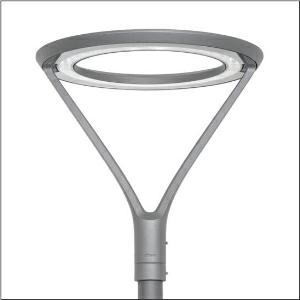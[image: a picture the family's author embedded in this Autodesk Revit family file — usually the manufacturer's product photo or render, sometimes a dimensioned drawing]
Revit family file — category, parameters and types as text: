
# Revit family: dl_r__20___st1_2a_5xa51283wa008_54be
name_source: partatom
category: Lighting Fixtures
units: mm (PartAtom-declared; Revit-internal decimal feet)

## family parameters
Cut with Voids When Loaded = No
Host = Face
Light Source = No
Part Type = Normal
Room Calculation Point = No
Round Connector Dimension = Use Diameter
Shared = No

## types (1)
- --- (1 x LED, 3040 lm, 24.6 W, 3000K)
    Apparent Load = 25 VA
    CIE Flux Codes = 32 72 97 100 100
    Color Rendering = 70
    Color Temperature = 3000K
    Default Elevation = 1800 mm
    Description = DL® 20, mast luminaire, primary light control with reflector, highly specular, primary optical cover: cover, of toughened safety glass of clear glass with excellent transmission level, light distribution: ST1.2a, light emission: direct distribution, primary light characteristic: asymmetric, installation type: post-top, LED, High Power LED, rated luminous flux: 3.020lm, luminous efficacy: 85lm/W, light colour: 730, colour temperature: 3000K, control gear: ECG Plus, control: overheat protection, power reduction, digital communication interface, constant luminous flux control, time-dependent luminous flux control, flexible luminous flux parameterisation, electronic power reduction, mains connection: 230..240V, 50/60Hz, connection cable pre-assembled, cable length: 5m, start of lifetime: 36W, end of service life: 36W, reduction: 17W, luminaire housing, upper part, of cast aluminium, powder-coated, Siteco® metallic grey (DB 702S), diameter: 690mm, height: 690mm, spigot size: 76mm (post-top), luminaire housing, of cast aluminium, powder-coated, Siteco® metallic grey (DB 702S), equipment: standard, protection rating (complete): IP66, insulation class (complete): insulation class II (safety insulation), certification: CE, ENEC, VDE, impact resistance: IK08, permissible operating ambient temperature: -25..+35°C, standard-compliant lighting for roads and squares, packaging unit: 1 piece

Light Distribution: ST1.2a
    Height = 690 mm
    Lamp = 1 x LED
    Lamp Light Flux = 3040 lm
    Lamp Power = 24.6 W
    Lamp count = 1
    Length = 690 mm
    Luminous efficacy = 124 lm/W
    Manufacturer = Siteco
    ModVariant = No
    Model = 5XA51283WA008
    Number of Poles = 1
    OnlyDefault = Yes
    Power Factor = 1
    Product Name = DL® 20 | ST1.2a
    Product group = mast luminaire | pylon top
    ProductGroupID = 6100
    Protection Class = Protection class II
    Protection Degree = IP 66
    RLX_Detail_Level = 1
    RLX_Emergency_Light_Flux = 0 lm
    RLX_Emergency_Type = 0
    RLX_Emergency_Type_DB = No
    RlxData = <blob elided: 206605 chars, md5=edea3e2a>
    Socket = socket
    Standby Power = 0 W
    System Light Flux = 3040 lm
    System Power = 25 W
    Type Comments = factory setting: luminous flux: 100 % | dim-lin: 254 | 330 mA
    Type Image = l_1006001.jpg
    URL = http://relux.com
    VarID = @adj_028391
    Voltage = 0 V
    Weight = 0.00 kg
    Width = 0 mm  [stored 0 ft]

note: [stored X ft] marks values corroborated as IEEE doubles in the binary element streams (Revit-internal decimal feet)

## geometry (parser evidence)
native form markers: Blend x4, Sweep x10
no freeform markers — native parametric forms only
